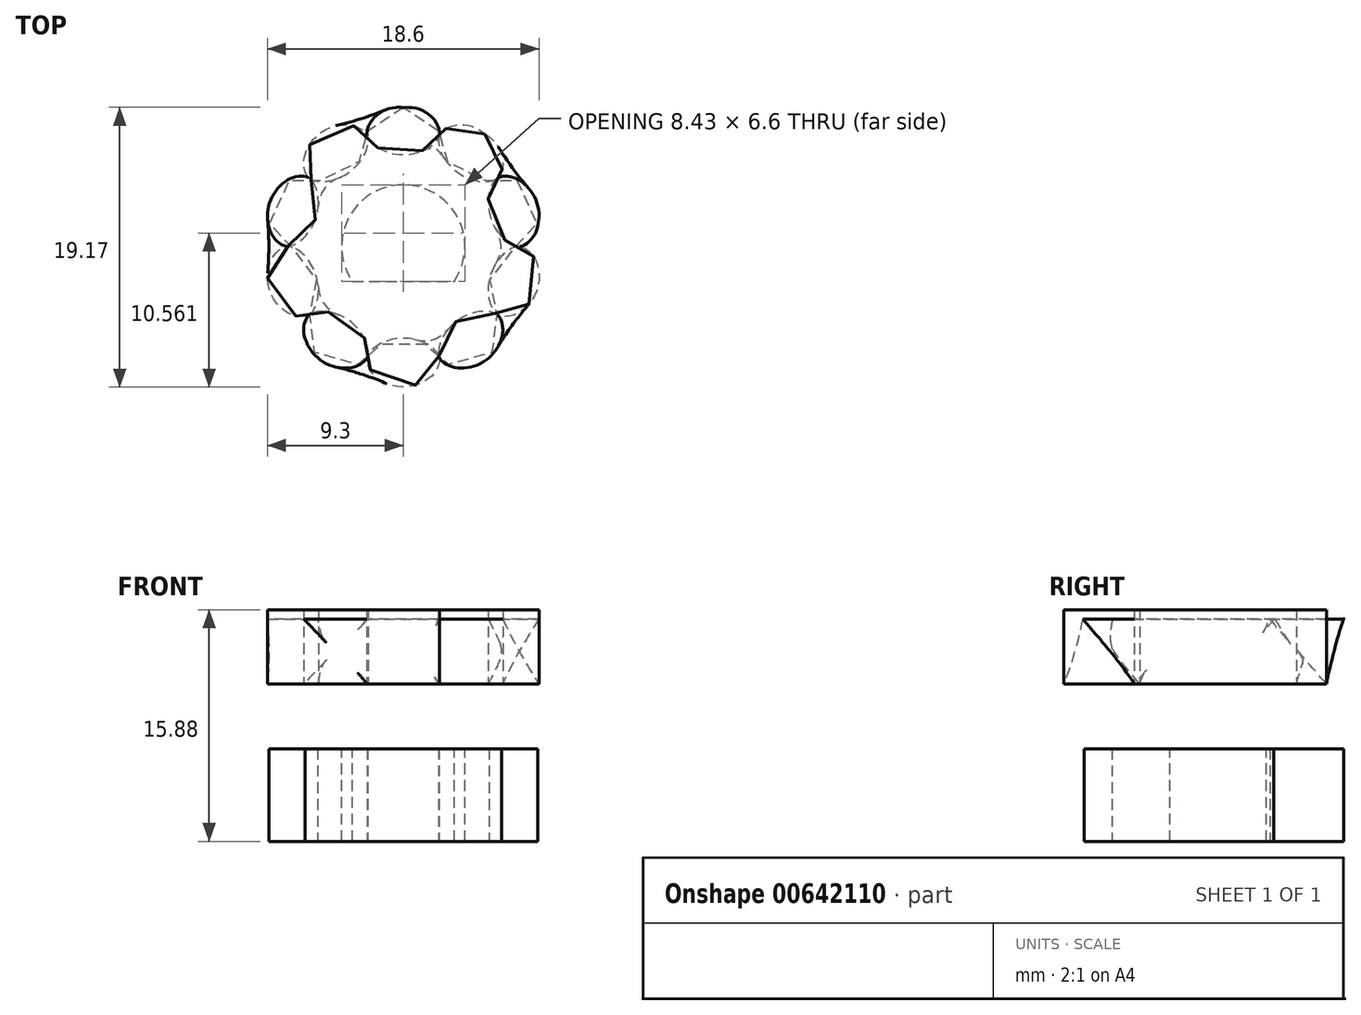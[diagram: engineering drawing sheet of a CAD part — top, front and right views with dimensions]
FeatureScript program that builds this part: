
annotation { "Feature Type Name" : "Feature", "Feature Type Description" : "" }
export const myFeature = defineFeature(function(context is Context, id is Id, definition is map)
    precondition{}
    {
        {
            var Q0;
            Q0=qCreatedBy(makeId("Top.planeOp"),FACE);
            var sketch = newSketch(context, id + "F0", { "sketchPlane" : qUnion([Q0])});
            skCircle(sketch, "E0", {"center": v(0, 0) * mm, "radius": 7.94 * mm, "construction": true});
            skCircle(sketch, "E1", {"center": v(0, 8.73) * mm, "radius": 0.8 * mm, "construction": true});
            skLineSegment(sketch, "E2", {"start": v(0, 9.52) * mm, "end": v(0, 8.73) * mm, "construction": true});
            skLineSegment(sketch, "E3", {"start": v(0, 0) * mm, "end": v(-4.2, 5.78) * mm, "construction": true});
            skCircle(sketch, "E4", {"center": v(-4.2, 5.78) * mm, "radius": 0.8 * mm, "construction": true});
            skLineSegment(sketch, "E5", {"start": v(0, 0) * mm, "end": v(0, 9.52) * mm, "construction": true});
            skCircle(sketch, "E6", {"center": v(0, 0) * mm, "radius": 9.53 * mm, "construction": true});
            skLineSegment(sketch, "E7", {"start": v(0, 0) * mm, "end": v(-2.45, 7.55) * mm, "construction": true});
            skLineSegment(sketch, "E8", {"start": v(0, 0) * mm, "end": v(-9.06, 2.94) * mm, "construction": true});
            skLineSegment(sketch, "E9", {"start": v(0, 0) * mm, "end": v(-6.42, 4.67) * mm, "construction": true});
            skCircle(sketch, "E10", {"center": v(-8.3, 2.7) * mm, "radius": 0.8 * mm, "construction": true});
            skCircle(sketch, "E11", {"center": v(-1.37, 8.62) * mm, "radius": 0.8 * mm, "construction": true});
            skCircle(sketch, "E12", {"center": v(-3.24, 6.37) * mm, "radius": 0.8 * mm, "construction": true});
            skLineSegment(sketch, "E13", {"start": v(-1.37, 8.62) * mm, "end": v(0, 0) * mm, "construction": true});
            skLineSegment(sketch, "E14", {"start": v(0, 0) * mm, "end": v(-3.24, 6.37) * mm, "construction": true});
            skLineSegment(sketch, "E15", {"start": v(-3.24, 6.37) * mm, "end": v(-2.54, 6.73) * mm, "construction": true});
            skLineSegment(sketch, "E16", {"start": v(-1.37, 8.62) * mm, "end": v(-2.15, 8.5) * mm, "construction": true});
            skPoint(sketch, "E17", {"position": v(-3.73, 5.14) * mm});
            skCircle(sketch, "E18", {"center": v(-5.05, 5.05) * mm, "radius": 0.8 * mm, "construction": true});
            skCircle(sketch, "E19", {"center": v(-7.78, 3.96) * mm, "radius": 0.8 * mm, "construction": true});
            skLineSegment(sketch, "E20", {"start": v(0, 0) * mm, "end": v(-5.05, 5.05) * mm, "construction": true});
            skLineSegment(sketch, "E21", {"start": v(0, 0) * mm, "end": v(-7.78, 3.96) * mm, "construction": true});
            skLineSegment(sketch, "E22", {"start": v(-5.05, 5.05) * mm, "end": v(-5.61, 4.5) * mm, "construction": true});
            skLineSegment(sketch, "E23", {"start": v(-7.78, 3.96) * mm, "end": v(-7.42, 4.67) * mm, "construction": true});
            skCircle(sketch, "E24", {"center": v(-0.69, 8.7) * mm, "radius": 0.8 * mm, "construction": true});
            skLineSegment(sketch, "E25", {"start": v(-0.69, 8.7) * mm, "end": v(0, 0) * mm, "construction": true});
            skCircle(sketch, "E26", {"center": v(-2.04, 8.5) * mm, "radius": 0.8 * mm, "construction": true});
            skLineSegment(sketch, "E27", {"start": v(-2.04, 8.5) * mm, "end": v(0, 0) * mm, "construction": true});
            skLineSegment(sketch, "E28", {"start": v(-0.69, 8.7) * mm, "end": v(-1.29, 9.22) * mm, "construction": true});
            skLineSegment(sketch, "E29", {"start": v(-2.04, 8.5) * mm, "end": v(-2.45, 7.81) * mm, "construction": true});
            skCircle(sketch, "E30", {"center": v(-2.73, 6.6) * mm, "radius": 0.8 * mm, "construction": true});
            skCircle(sketch, "E31", {"center": v(-3.73, 6.1) * mm, "radius": 0.8 * mm, "construction": true});
            skLineSegment(sketch, "E32", {"start": v(-2.73, 6.6) * mm, "end": v(0, 0) * mm, "construction": true});
            skLineSegment(sketch, "E33", {"start": v(-2.73, 6.6) * mm, "end": v(-2.43, 7.33) * mm, "construction": true});
            skLineSegment(sketch, "E34", {"start": v(-3.73, 6.1) * mm, "end": v(0, 0) * mm, "construction": true});
            skLineSegment(sketch, "E35", {"start": v(-3.73, 6.1) * mm, "end": v(-2.96, 5.9) * mm, "construction": true});
            skCircle(sketch, "E36", {"center": v(-4.64, 5.43) * mm, "radius": 0.8 * mm, "construction": true});
            skLineSegment(sketch, "E37", {"start": v(-4.64, 5.43) * mm, "end": v(0, 0) * mm, "construction": true});
            skLineSegment(sketch, "E38", {"start": v(-4.64, 5.43) * mm, "end": v(-4.7, 4.64) * mm, "construction": true});
            skCircle(sketch, "E39", {"center": v(-5.43, 4.64) * mm, "radius": 0.8 * mm, "construction": true});
            skCircle(sketch, "E40", {"center": v(-7.44, 4.56) * mm, "radius": 0.8 * mm, "construction": true});
            skCircle(sketch, "E41", {"center": v(-8.07, 3.34) * mm, "radius": 0.8 * mm, "construction": true});
            skLineSegment(sketch, "E42", {"start": v(-5.43, 4.64) * mm, "end": v(0, 0) * mm, "construction": true});
            skLineSegment(sketch, "E43", {"start": v(-5.43, 4.64) * mm, "end": v(-6.22, 4.58) * mm, "construction": true});
            skLineSegment(sketch, "E44", {"start": v(-7.44, 4.56) * mm, "end": v(0, 0) * mm, "construction": true});
            skLineSegment(sketch, "E45", {"start": v(-8.07, 3.34) * mm, "end": v(0, 0) * mm, "construction": true});
            skLineSegment(sketch, "E46", {"start": v(-7.44, 4.56) * mm, "end": v(-6.67, 4.75) * mm, "construction": true});
            skLineSegment(sketch, "E47", {"start": v(-8.07, 3.34) * mm, "end": v(-8.37, 4.07) * mm, "construction": true});
            skSolve(sketch);
        }
        {
            var Q0;
            Q0=qCreatedBy(makeId("Top.planeOp"),FACE);
            var sketch = newSketch(context, id + "F1", { "sketchPlane" : qUnion([Q0])});
            skPoint(sketch, "E48.0", {"position": v(0, 9.52) * mm});
            skPoint(sketch, "E48.1", {"position": v(-1.29, 9.22) * mm});
            skPoint(sketch, "E48.2", {"position": v(-2.15, 8.5) * mm});
            skPoint(sketch, "E48.3", {"position": v(-2.45, 7.81) * mm});
            skPoint(sketch, "E48.4", {"position": v(-2.45, 7.55) * mm});
            skPoint(sketch, "E48.5", {"position": v(-2.43, 7.33) * mm});
            skPoint(sketch, "E48.6", {"position": v(-2.54, 6.73) * mm});
            skPoint(sketch, "E48.7", {"position": v(-2.96, 5.9) * mm});
            skPoint(sketch, "E48.8", {"position": v(-3.73, 5.14) * mm});
            skPoint(sketch, "E48.9", {"position": v(-4.7, 4.64) * mm});
            skPoint(sketch, "E48.10", {"position": v(-5.61, 4.5) * mm});
            skPoint(sketch, "E48.11", {"position": v(-6.22, 4.58) * mm});
            skPoint(sketch, "E48.12", {"position": v(-6.42, 4.67) * mm});
            skPoint(sketch, "E48.13", {"position": v(-6.67, 4.75) * mm});
            skPoint(sketch, "E48.14", {"position": v(-7.42, 4.67) * mm});
            skPoint(sketch, "E48.15", {"position": v(-8.37, 4.07) * mm});
            skPoint(sketch, "E48.16", {"position": v(-9.06, 2.94) * mm});
            skLineSegment(sketch, "E49.0", {"start": v(0, 0) * mm, "end": v(0, 9.52) * mm, "construction": true});
            skLineSegment(sketch, "E49.1", {"start": v(0, 0) * mm, "end": v(-4.2, 5.78) * mm, "construction": true});
            skLineSegment(sketch, "E50.0", {"start": v(0, 0) * mm, "end": v(-9.06, 2.94) * mm, "construction": true});
            skPoint(sketch, "E51.1.1", {"position": v(-9.17, 1.62) * mm});
            skPoint(sketch, "E51.1.2", {"position": v(-8.75, 0.58) * mm});
            skPoint(sketch, "E51.1.3", {"position": v(-8.19, 0.08) * mm});
            skPoint(sketch, "E51.1.4", {"position": v(-7.94, 0) * mm});
            skPoint(sketch, "E51.1.5", {"position": v(-7.73, -0.04) * mm});
            skPoint(sketch, "E51.1.6", {"position": v(-7.18, -0.33) * mm});
            skPoint(sketch, "E51.1.7", {"position": v(-6.53, -1) * mm});
            skPoint(sketch, "E51.1.8", {"position": v(-6.04, -1.96) * mm});
            skPoint(sketch, "E51.1.9", {"position": v(-5.87, -3.04) * mm});
            skPoint(sketch, "E51.1.10", {"position": v(-6, -3.95) * mm});
            skPoint(sketch, "E51.1.11", {"position": v(-6.28, -4.5) * mm});
            skPoint(sketch, "E51.1.12", {"position": v(-6.42, -4.67) * mm});
            skPoint(sketch, "E51.1.13", {"position": v(-6.58, -4.88) * mm});
            skPoint(sketch, "E51.1.14", {"position": v(-6.74, -5.61) * mm});
            skPoint(sketch, "E51.1.15", {"position": v(-6.46, -6.7) * mm});
            skPoint(sketch, "E51.2.0", {"position": v(-5.6, -7.7) * mm});
            skPoint(sketch, "E51.2.1", {"position": v(-4.38, -8.22) * mm});
            skPoint(sketch, "E51.2.2", {"position": v(-3.26, -8.14) * mm});
            skPoint(sketch, "E51.2.3", {"position": v(-2.6, -7.76) * mm});
            skPoint(sketch, "E51.2.4", {"position": v(-2.45, -7.55) * mm});
            skPoint(sketch, "E51.2.5", {"position": v(-2.34, -7.36) * mm});
            skPoint(sketch, "E51.2.6", {"position": v(-1.9, -6.93) * mm});
            skPoint(sketch, "E51.2.7", {"position": v(-1.08, -6.52) * mm});
            skPoint(sketch, "E51.2.8", {"position": v(0, -6.35) * mm});
            skPoint(sketch, "E51.2.9", {"position": v(1.08, -6.52) * mm});
            skPoint(sketch, "E51.2.10", {"position": v(1.9, -6.93) * mm});
            skPoint(sketch, "E51.2.11", {"position": v(2.34, -7.36) * mm});
            skPoint(sketch, "E51.2.12", {"position": v(2.45, -7.55) * mm});
            skPoint(sketch, "E51.2.13", {"position": v(2.6, -7.76) * mm});
            skPoint(sketch, "E51.2.14", {"position": v(3.26, -8.14) * mm});
            skPoint(sketch, "E51.2.15", {"position": v(4.38, -8.22) * mm});
            skPoint(sketch, "E51.3.0", {"position": v(5.6, -7.7) * mm});
            skPoint(sketch, "E51.3.1", {"position": v(6.46, -6.7) * mm});
            skPoint(sketch, "E51.3.2", {"position": v(6.74, -5.61) * mm});
            skPoint(sketch, "E51.3.3", {"position": v(6.58, -4.88) * mm});
            skPoint(sketch, "E51.3.4", {"position": v(6.42, -4.67) * mm});
            skPoint(sketch, "E51.3.5", {"position": v(6.28, -4.5) * mm});
            skPoint(sketch, "E51.3.6", {"position": v(6, -3.95) * mm});
            skPoint(sketch, "E51.3.7", {"position": v(5.87, -3.04) * mm});
            skPoint(sketch, "E51.3.8", {"position": v(6.04, -1.96) * mm});
            skPoint(sketch, "E51.3.9", {"position": v(6.53, -1) * mm});
            skPoint(sketch, "E51.3.10", {"position": v(7.18, -0.33) * mm});
            skPoint(sketch, "E51.3.11", {"position": v(7.73, -0.04) * mm});
            skPoint(sketch, "E51.3.12", {"position": v(7.94, 0) * mm});
            skPoint(sketch, "E51.3.13", {"position": v(8.19, 0.08) * mm});
            skPoint(sketch, "E51.3.14", {"position": v(8.75, 0.58) * mm});
            skPoint(sketch, "E51.3.15", {"position": v(9.17, 1.62) * mm});
            skPoint(sketch, "E51.4.0", {"position": v(9.06, 2.94) * mm});
            skPoint(sketch, "E51.4.1", {"position": v(8.37, 4.07) * mm});
            skPoint(sketch, "E51.4.2", {"position": v(7.42, 4.67) * mm});
            skPoint(sketch, "E51.4.3", {"position": v(6.67, 4.75) * mm});
            skPoint(sketch, "E51.4.4", {"position": v(6.42, 4.67) * mm});
            skPoint(sketch, "E51.4.5", {"position": v(6.22, 4.58) * mm});
            skPoint(sketch, "E51.4.6", {"position": v(5.61, 4.5) * mm});
            skPoint(sketch, "E51.4.7", {"position": v(4.7, 4.64) * mm});
            skPoint(sketch, "E51.4.8", {"position": v(3.73, 5.14) * mm});
            skPoint(sketch, "E51.4.9", {"position": v(2.96, 5.9) * mm});
            skPoint(sketch, "E51.4.10", {"position": v(2.54, 6.73) * mm});
            skPoint(sketch, "E51.4.11", {"position": v(2.43, 7.33) * mm});
            skPoint(sketch, "E51.4.12", {"position": v(2.45, 7.55) * mm});
            skPoint(sketch, "E51.4.13", {"position": v(2.45, 7.81) * mm});
            skPoint(sketch, "E51.4.14", {"position": v(2.15, 8.5) * mm});
            skPoint(sketch, "E51.4.15", {"position": v(1.29, 9.22) * mm});
            skPoint(sketch, "E51.center", {"position": v(0, 0) * mm});
            skFitSpline(sketch, "E52", {"points": [v(0, 9.52) * mm, v(-1.29, 9.22) * mm, v(-2.15, 8.5) * mm, v(-2.45, 7.81) * mm, v(-2.45, 7.55) * mm, v(-2.43, 7.33) * mm, v(-2.54, 6.73) * mm, v(-2.96, 5.9) * mm, v(-3.73, 5.14) * mm, v(-4.7, 4.64) * mm, v(-5.61, 4.5) * mm, v(-6.22, 4.58) * mm, v(-6.42, 4.67) * mm, v(-6.67, 4.75) * mm, v(-7.42, 4.67) * mm, v(-8.37, 4.07) * mm, v(-9.06, 2.94) * mm, v(-9.17, 1.62) * mm, v(-8.75, 0.58) * mm, v(-8.19, 0.08) * mm, v(-7.94, 0) * mm, v(-7.73, -0.04) * mm, v(-7.18, -0.33) * mm, v(-6.53, -1) * mm, v(-6.04, -1.96) * mm, v(-5.87, -3.04) * mm, v(-6, -3.95) * mm, v(-6.28, -4.5) * mm, v(-6.42, -4.67) * mm, v(-6.58, -4.88) * mm, v(-6.74, -5.61) * mm, v(-6.46, -6.7) * mm, v(-5.6, -7.7) * mm, v(-4.38, -8.22) * mm, v(-3.26, -8.14) * mm, v(-2.6, -7.76) * mm, v(-2.45, -7.55) * mm, v(-2.34, -7.36) * mm, v(-1.9, -6.93) * mm, v(-1.08, -6.52) * mm, v(0, -6.35) * mm, v(1.08, -6.52) * mm, v(1.9, -6.93) * mm, v(2.34, -7.36) * mm, v(2.45, -7.55) * mm, v(2.6, -7.76) * mm, v(3.26, -8.14) * mm, v(4.38, -8.22) * mm, v(5.6, -7.7) * mm, v(6.46, -6.7) * mm, v(6.74, -5.61) * mm, v(6.58, -4.88) * mm, v(6.42, -4.67) * mm, v(6.28, -4.5) * mm, v(6, -3.95) * mm, v(5.87, -3.04) * mm, v(6.04, -1.96) * mm, v(6.53, -1) * mm, v(7.18, -0.33) * mm, v(7.73, -0.04) * mm, v(7.94, 0) * mm, v(8.19, 0.08) * mm, v(8.75, 0.58) * mm, v(9.17, 1.62) * mm, v(9.06, 2.94) * mm, v(8.37, 4.07) * mm, v(7.42, 4.67) * mm, v(6.67, 4.75) * mm, v(6.42, 4.67) * mm, v(6.22, 4.58) * mm, v(5.61, 4.5) * mm, v(4.7, 4.64) * mm, v(3.73, 5.14) * mm, v(2.96, 5.9) * mm, v(2.54, 6.73) * mm, v(2.43, 7.33) * mm, v(2.45, 7.55) * mm, v(2.45, 7.81) * mm, v(2.15, 8.5) * mm, v(1.29, 9.22) * mm, v(0, 9.52) * mm]});
            skSolve(sketch);
        }
        {
            var Q0;
            Q0=makeQuery(id+"F1.imprint","IMPRINT",FACE,{"disambiguationData":[TD([[makeQuery(id+"F1.imprint","IMPRINT",EDGE,{"derivedFrom":sQuery(id+"F1.wireOp",EDGE,"E52")}),1.0]])]});
            extrude(context, id + "F2", {"entities" : qUnion([Q0]), "depth" : 6.35 * mm, "offsetDistance" : 25.4 * mm});
        }
        {
            var Q0;
            Q0=makeQuery(id+"F2.opExtrude","CAP_FACE",FACE,{"disambiguationData":[OSD([sQuery(id+"F1.wireOp",EDGE,"E52")])],"isStart":false});
            var sketch = newSketch(context, id + "F3", { "sketchPlane" : qUnion([Q0])});
            skCircle(sketch, "E53", {"center": v(0, 0) * mm, "radius": 4.22 * mm});
            skLineSegment(sketch, "E54", {"start": v(-3.49, -2.38) * mm, "end": v(3.49, -2.38) * mm});
            skSolve(sketch);
        }
        {
            var Q0;
            {var subQ0=sQuery(id+"F3.wireOp",EDGE,"E54");Q0=makeQuery(id+"F3.imprint","IMPRINT",FACE,{"disambiguationData":[TD([[makeQuery(id+"F3.imprint","IMPRINT",EDGE,{"derivedFrom":subQ0}),1.0]])]});}
            extrude(context, id + "F4", {"entities" : qUnion([Q0]), "operationType" : NewBodyOperationType.REMOVE, "endBound" : BoundingType.THROUGH_ALL, "oppositeDirection" : true, "depth" : 25.4 * mm, "offsetDistance" : 25.4 * mm});
        }
        {
            var Q0;
            Q0=makeQuery(id+"F2.opExtrude","CAP_FACE",FACE,{"disambiguationData":[OSD([sQuery(id+"F1.wireOp",EDGE,"E52")])],"isStart":false});
            cPlane(context, id + "F5", {"entities" : qUnion([Q0]), "cplaneType" : CPlaneType.OFFSET, "offset" : 4.44 * mm, "width" : 152.4 * mm, "height" : 152.4 * mm});
        }
        {
            var Q0;
            Q0=qCreatedBy(id+"F5.planeOp",FACE);
            var sketch = newSketch(context, id + "F6", { "sketchPlane" : qUnion([Q0])});
            skFitSpline(sketch, "E55.0.0", {"points": [v(0, 9.52) * mm, v(-0.45, 9.52) * mm, v(-1.32, 9.31) * mm, v(-2.2, 8.59) * mm, v(-2.48, 7.84) * mm, v(-2.46, 7.55) * mm, v(-2.4, 7.32) * mm, v(-2.5, 6.67) * mm, v(-2.93, 5.87) * mm, v(-3.7, 5.09) * mm, v(-4.67, 4.6) * mm, v(-5.57, 4.45) * mm, v(-6.22, 4.55) * mm, v(-6.42, 4.67) * mm, v(-6.69, 4.79) * mm, v(-7.49, 4.74) * mm, v(-8.45, 4.13) * mm, v(-9.16, 2.98) * mm, v(-9.26, 1.62) * mm, v(-8.84, 0.57) * mm, v(-8.22, 0.06) * mm, v(-7.94, 0) * mm, v(-7.7, -0.03) * mm, v(-7.12, -0.32) * mm, v(-6.48, -0.97) * mm, v(-5.98, -1.94) * mm, v(-5.82, -3.03) * mm, v(-5.95, -3.93) * mm, v(-6.25, -4.5) * mm, v(-6.42, -4.66) * mm, v(-6.62, -4.88) * mm, v(-6.82, -5.66) * mm, v(-6.54, -6.76) * mm, v(-5.66, -7.8) * mm, v(-4.4, -8.3) * mm, v(-3.27, -8.23) * mm, v(-2.6, -7.8) * mm, v(-2.45, -7.55) * mm, v(-2.35, -7.34) * mm, v(-1.9, -6.87) * mm, v(-1.08, -6.47) * mm, v(0, -6.29) * mm, v(1.08, -6.47) * mm, v(1.9, -6.87) * mm, v(2.35, -7.34) * mm, v(2.45, -7.55) * mm, v(2.6, -7.8) * mm, v(3.27, -8.23) * mm, v(4.4, -8.3) * mm, v(5.66, -7.8) * mm, v(6.54, -6.76) * mm, v(6.82, -5.66) * mm, v(6.62, -4.88) * mm, v(6.42, -4.66) * mm, v(6.25, -4.5) * mm, v(5.95, -3.93) * mm, v(5.82, -3.03) * mm, v(5.98, -1.94) * mm, v(6.48, -0.97) * mm, v(7.12, -0.32) * mm, v(7.7, -0.03) * mm, v(7.94, 0) * mm, v(8.22, 0.06) * mm, v(8.84, 0.57) * mm, v(9.26, 1.62) * mm, v(9.16, 2.98) * mm, v(8.45, 4.13) * mm, v(7.49, 4.74) * mm, v(6.69, 4.79) * mm, v(6.42, 4.67) * mm, v(6.22, 4.55) * mm, v(5.57, 4.45) * mm, v(4.67, 4.6) * mm, v(3.7, 5.09) * mm, v(2.93, 5.87) * mm, v(2.5, 6.67) * mm, v(2.4, 7.32) * mm, v(2.46, 7.55) * mm, v(2.48, 7.84) * mm, v(2.2, 8.59) * mm, v(1.32, 9.31) * mm, v(0.45, 9.52) * mm, v(0, 9.52) * mm]});
            skSolve(sketch);
        }
        {
            var Q0;
            Q0=makeQuery(id+"F6.imprint","IMPRINT",FACE,{"disambiguationData":[TD([[makeQuery(id+"F6.imprint","IMPRINT",EDGE,{"derivedFrom":sQuery(id+"F6.wireOp",EDGE,"E55.0.0")}),1.0]])]});
            extrude(context, id + "F7", {"entities" : qUnion([Q0]), "depth" : 5.08 * mm, "offsetDistance" : 25.4 * mm});
        }
        {
            var Q0;
            Q0=qCreatedBy(id+"F5.planeOp",FACE);
            cPlane(context, id + "F8", {"entities" : qUnion([Q0]), "cplaneType" : CPlaneType.OFFSET, "offset" : 4.44 * mm, "width" : 152.4 * mm, "height" : 152.4 * mm});
        }
        {
            var Q0;
            Q0=qCreatedBy(id+"F8.planeOp",FACE);
            var sketch = newSketch(context, id + "F9", { "sketchPlane" : qUnion([Q0])});
            skFitSpline(sketch, "E56.0.0", {"points": [v(0, 9.52) * mm, v(0.45, 9.52) * mm, v(1.32, 9.31) * mm, v(2.2, 8.59) * mm, v(2.48, 7.84) * mm, v(2.46, 7.55) * mm, v(2.4, 7.32) * mm, v(2.5, 6.67) * mm, v(2.93, 5.87) * mm, v(3.7, 5.09) * mm, v(4.67, 4.6) * mm, v(5.57, 4.45) * mm, v(6.22, 4.55) * mm, v(6.42, 4.67) * mm, v(6.69, 4.79) * mm, v(7.49, 4.74) * mm, v(8.45, 4.13) * mm, v(9.16, 2.98) * mm, v(9.26, 1.62) * mm, v(8.84, 0.57) * mm, v(8.22, 0.06) * mm, v(7.94, 0) * mm, v(7.7, -0.03) * mm, v(7.12, -0.32) * mm, v(6.48, -0.97) * mm, v(5.98, -1.94) * mm, v(5.82, -3.03) * mm, v(5.95, -3.93) * mm, v(6.25, -4.5) * mm, v(6.42, -4.66) * mm, v(6.62, -4.88) * mm, v(6.82, -5.66) * mm, v(6.54, -6.76) * mm, v(5.66, -7.8) * mm, v(4.4, -8.3) * mm, v(3.27, -8.23) * mm, v(2.6, -7.8) * mm, v(2.45, -7.55) * mm, v(2.35, -7.34) * mm, v(1.9, -6.87) * mm, v(1.08, -6.47) * mm, v(0, -6.29) * mm, v(-1.08, -6.47) * mm, v(-1.9, -6.87) * mm, v(-2.35, -7.34) * mm, v(-2.45, -7.55) * mm, v(-2.6, -7.8) * mm, v(-3.27, -8.23) * mm, v(-4.4, -8.3) * mm, v(-5.66, -7.8) * mm, v(-6.54, -6.76) * mm, v(-6.82, -5.66) * mm, v(-6.62, -4.88) * mm, v(-6.42, -4.66) * mm, v(-6.25, -4.5) * mm, v(-5.95, -3.93) * mm, v(-5.82, -3.03) * mm, v(-5.98, -1.94) * mm, v(-6.48, -0.97) * mm, v(-7.12, -0.32) * mm, v(-7.7, -0.03) * mm, v(-7.94, 0) * mm, v(-8.22, 0.06) * mm, v(-8.84, 0.57) * mm, v(-9.26, 1.62) * mm, v(-9.16, 2.98) * mm, v(-8.45, 4.13) * mm, v(-7.49, 4.74) * mm, v(-6.69, 4.79) * mm, v(-6.42, 4.67) * mm, v(-6.22, 4.55) * mm, v(-5.57, 4.45) * mm, v(-4.67, 4.6) * mm, v(-3.7, 5.09) * mm, v(-2.93, 5.87) * mm, v(-2.5, 6.67) * mm, v(-2.4, 7.32) * mm, v(-2.46, 7.55) * mm, v(-2.48, 7.84) * mm, v(-2.2, 8.59) * mm, v(-1.32, 9.31) * mm, v(-0.45, 9.52) * mm, v(0, 9.52) * mm]});
            skSolve(sketch);
        }
        {
            var Q0;
            Q0=makeQuery(id+"F7.opExtrude","SWEPT_BODY",BODY,{"disambiguationData":[OSD([sQuery(id+"F6.wireOp",EDGE,"E55.0.0")])]});
            var Q1;
            Q1=makeQuery(id+"F4.boolean.opBoolean","COPY",FACE,{"derivedFrom":makeQuery(id+"F4.opExtrude","SWEPT_FACE",FACE,{"disambiguationData":[OSD([sQuery(id+"F3.wireOp",EDGE,"E53")])]})});
            transform(context, id + "F10", {"entities" : qUnion([Q0]), "transformType" : TransformType.ROTATION, "transformAxis" : qUnion([Q1]), "angle" : 36 * degree, "makeCopy" : false});
        }
        {
            var Q0;
            Q0=qCreatedBy(id+"F5.planeOp",FACE);
            var sketch = newSketch(context, id + "F11", { "sketchPlane" : qUnion([Q0])});
            skFitSpline(sketch, "E57.0.0", {"points": [v(5.6, 7.7) * mm, v(5.96, 7.44) * mm, v(6.54, 6.76) * mm, v(6.82, 5.66) * mm, v(6.62, 4.88) * mm, v(6.42, 4.66) * mm, v(6.25, 4.5) * mm, v(5.95, 3.93) * mm, v(5.82, 3.03) * mm, v(5.98, 1.94) * mm, v(6.48, 0.97) * mm, v(7.12, 0.32) * mm, v(7.7, 0.03) * mm, v(7.94, 0) * mm, v(8.22, -0.06) * mm, v(8.84, -0.57) * mm, v(9.26, -1.62) * mm, v(9.16, -2.98) * mm, v(8.45, -4.13) * mm, v(7.49, -4.74) * mm, v(6.69, -4.79) * mm, v(6.42, -4.67) * mm, v(6.22, -4.55) * mm, v(5.57, -4.45) * mm, v(4.67, -4.6) * mm, v(3.7, -5.09) * mm, v(2.93, -5.87) * mm, v(2.5, -6.67) * mm, v(2.4, -7.32) * mm, v(2.46, -7.55) * mm, v(2.48, -7.84) * mm, v(2.2, -8.59) * mm, v(1.32, -9.31) * mm, v(0, -9.64) * mm, v(-1.32, -9.31) * mm, v(-2.2, -8.59) * mm, v(-2.48, -7.84) * mm, v(-2.46, -7.55) * mm, v(-2.4, -7.32) * mm, v(-2.5, -6.67) * mm, v(-2.93, -5.87) * mm, v(-3.7, -5.09) * mm, v(-4.67, -4.6) * mm, v(-5.57, -4.45) * mm, v(-6.22, -4.55) * mm, v(-6.42, -4.67) * mm, v(-6.69, -4.79) * mm, v(-7.49, -4.74) * mm, v(-8.45, -4.13) * mm, v(-9.16, -2.98) * mm, v(-9.26, -1.62) * mm, v(-8.84, -0.57) * mm, v(-8.22, -0.06) * mm, v(-7.94, 0) * mm, v(-7.7, 0.03) * mm, v(-7.12, 0.32) * mm, v(-6.48, 0.97) * mm, v(-5.98, 1.94) * mm, v(-5.82, 3.03) * mm, v(-5.95, 3.93) * mm, v(-6.25, 4.5) * mm, v(-6.42, 4.66) * mm, v(-6.62, 4.88) * mm, v(-6.82, 5.66) * mm, v(-6.54, 6.76) * mm, v(-5.66, 7.8) * mm, v(-4.4, 8.3) * mm, v(-3.27, 8.23) * mm, v(-2.6, 7.8) * mm, v(-2.45, 7.55) * mm, v(-2.35, 7.34) * mm, v(-1.9, 6.87) * mm, v(-1.08, 6.47) * mm, v(0, 6.29) * mm, v(1.08, 6.47) * mm, v(1.9, 6.87) * mm, v(2.35, 7.34) * mm, v(2.45, 7.55) * mm, v(2.6, 7.8) * mm, v(3.27, 8.23) * mm, v(4.4, 8.3) * mm, v(5.23, 7.97) * mm, v(5.6, 7.7) * mm]});
            skSolve(sketch);
        }
        {
            var Q0;
            Q0=makeQuery(id+"F11.imprint","IMPRINT",FACE,{"disambiguationData":[TD([[makeQuery(id+"F11.imprint","IMPRINT",EDGE,{"derivedFrom":sQuery(id+"F11.wireOp",EDGE,"E57.0.0")}),-1.0]])]});
            var Q1;
            Q1=makeQuery(id+"F9.imprint","IMPRINT",FACE,{"disambiguationData":[TD([[makeQuery(id+"F9.imprint","IMPRINT",EDGE,{"derivedFrom":sQuery(id+"F9.wireOp",EDGE,"E56.0.0")}),-1.0]])]});
            loft(context, id + "F12", {"sheetProfilesArray" : [{ "sheetProfileEntities" : qUnion([Q0]) }, { "sheetProfileEntities" : qUnion([Q1]) }]});
        }
    });
